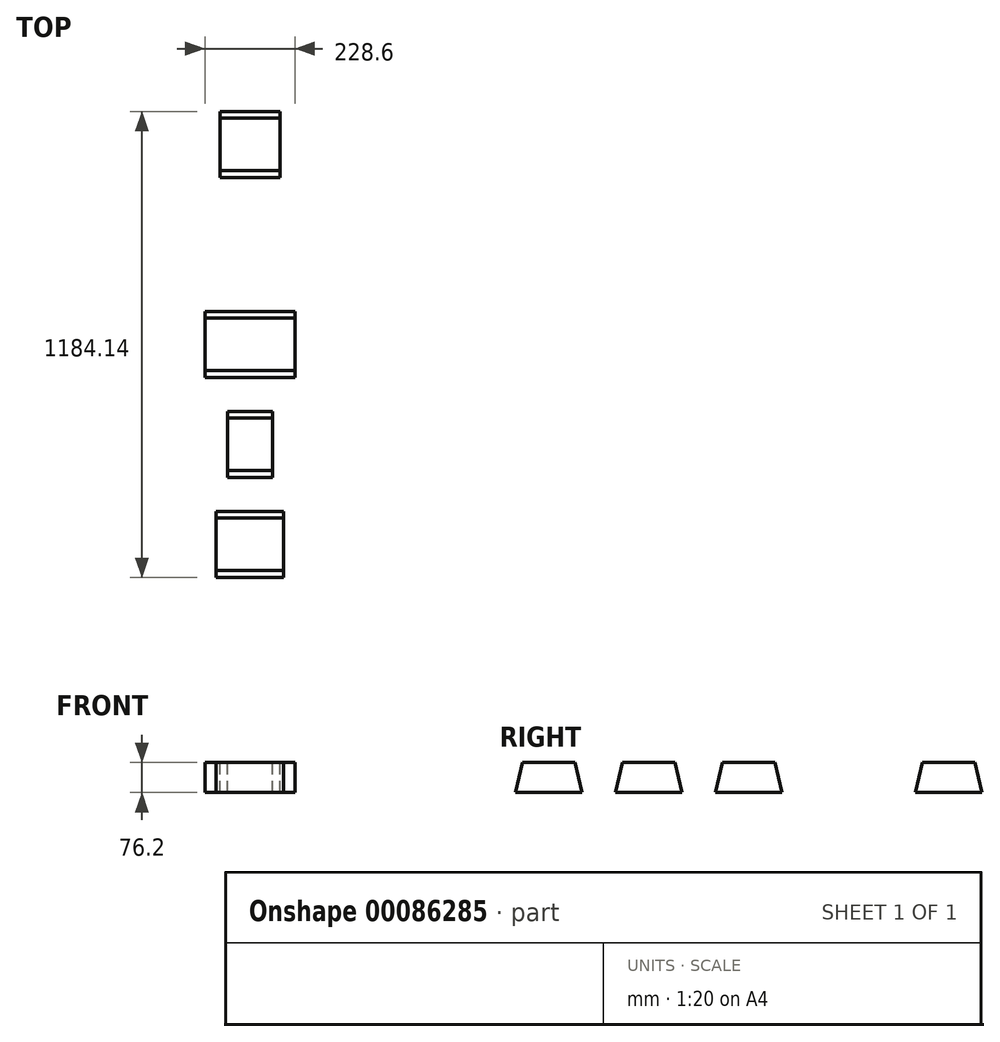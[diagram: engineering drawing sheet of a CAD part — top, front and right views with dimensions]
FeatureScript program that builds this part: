
annotation { "Feature Type Name" : "Feature", "Feature Type Description" : "" }
export const myFeature = defineFeature(function(context is Context, id is Id, definition is map)
    precondition{}
    {
        {
            var Q0;
            Q0=qCreatedBy(makeId("Top.planeOp"),FACE);
            var sketch = newSketch(context, id + "F0", { "sketchPlane" : qUnion([Q0])});
            skLineSegment(sketch, "E0.bottom", {"start": v(114.3, -84.07) * mm, "end": v(-114.3, -84.07) * mm});
            skLineSegment(sketch, "E0.top", {"start": v(114.3, 84.07) * mm, "end": v(-114.3, 84.07) * mm});
            skLineSegment(sketch, "E0.left", {"start": v(114.3, -84.07) * mm, "end": v(114.3, 84.07) * mm});
            skLineSegment(sketch, "E0.right", {"start": v(-114.3, -84.07) * mm, "end": v(-114.3, 84.07) * mm});
            skPoint(sketch, "E0.middle", {"position": v(0, 0) * mm});
            skLineSegment(sketch, "E1", {"start": v(0, 84.07) * mm, "end": v(0, -84.07) * mm, "construction": true});
            skLineSegment(sketch, "E2.bottom", {"start": v(-57.15, -169.93) * mm, "end": v(57.15, -169.93) * mm});
            skLineSegment(sketch, "E2.top", {"start": v(-57.15, -338.07) * mm, "end": v(57.15, -338.07) * mm});
            skLineSegment(sketch, "E2.left", {"start": v(-57.15, -169.93) * mm, "end": v(-57.15, -338.07) * mm});
            skLineSegment(sketch, "E2.right", {"start": v(57.15, -169.93) * mm, "end": v(57.15, -338.07) * mm});
            skPoint(sketch, "E2.middle", {"position": v(0, -254) * mm});
            skLineSegment(sketch, "E3", {"start": v(0, 0) * mm, "end": v(-114.3, 0) * mm, "construction": true});
            skLineSegment(sketch, "E4", {"start": v(-57.15, 0) * mm, "end": v(-57.15, -84.07) * mm, "construction": true});
            skLineSegment(sketch, "E5", {"start": v(-57.15, -42.04) * mm, "end": v(114.3, -42.04) * mm, "construction": true});
            skLineSegment(sketch, "E6.bottom", {"start": v(-85.72, -423.93) * mm, "end": v(85.73, -423.93) * mm});
            skLineSegment(sketch, "E6.top", {"start": v(-85.73, -592.07) * mm, "end": v(85.73, -592.07) * mm});
            skLineSegment(sketch, "E6.left", {"start": v(-85.72, -423.93) * mm, "end": v(-85.73, -592.07) * mm});
            skLineSegment(sketch, "E6.right", {"start": v(85.73, -423.93) * mm, "end": v(85.73, -592.07) * mm});
            skPoint(sketch, "E6.middle", {"position": v(0, -508) * mm});
            skPoint(sketch, "E6.middle.positionSnap0", {"position": v(0, -338.07) * mm});
            skPoint(sketch, "E6.centerSnap0", {"position": v(0, -338.07) * mm});
            skLineSegment(sketch, "E7", {"start": v(-38.1, 84.07) * mm, "end": v(-38.1, -84.07) * mm, "construction": true});
            skLineSegment(sketch, "E8", {"start": v(38.1, 84.07) * mm, "end": v(38.1, -84.07) * mm, "construction": true});
            skLineSegment(sketch, "E9", {"start": v(-114.3, 38.22) * mm, "end": v(-38.1, 38.22) * mm, "construction": true});
            skLineSegment(sketch, "E10", {"start": v(-38.1, 38.22) * mm, "end": v(38.1, 38.22) * mm, "construction": true});
            skLineSegment(sketch, "E11", {"start": v(38.1, 38.22) * mm, "end": v(114.3, 38.22) * mm, "construction": true});
            skLineSegment(sketch, "E12.bottom", {"start": v(76.2, 423.93) * mm, "end": v(0, 423.93) * mm});
            skLineSegment(sketch, "E12.top", {"start": v(76.2, 592.07) * mm, "end": v(-76.2, 592.07) * mm});
            skLineSegment(sketch, "E12.left", {"start": v(76.2, 423.93) * mm, "end": v(76.2, 592.07) * mm});
            skLineSegment(sketch, "E12.right", {"start": v(-76.2, 423.93) * mm, "end": v(-76.2, 592.07) * mm});
            skPoint(sketch, "E12.middle", {"position": v(0, 508) * mm});
            skLineSegment(sketch, "E13", {"start": v(0, 592.07) * mm, "end": v(0, 423.93) * mm, "construction": true});
            skLineSegment(sketch, "E14", {"start": v(0, 423.93) * mm, "end": v(-76.2, 423.93) * mm});
            skSolve(sketch);
        }
        {
            var Q0;
            Q0=makeQuery(id+"F0.imprint","IMPRINT",FACE,{"disambiguationData":[TD([[makeQuery(id+"F0.imprint","IMPRINT",EDGE,{"derivedFrom":sQuery(id+"F0.wireOp",EDGE,"E0.bottom")}),-1.0]])]});
            cPlane(context, id + "F1", {"entities" : qUnion([Q0]), "cplaneType" : CPlaneType.OFFSET, "offset" : 76.2 * mm, "width" : 152.4 * mm, "height" : 152.4 * mm});
        }
        {
            var Q0;
            Q0=qCreatedBy(id+"F1.planeOp",FACE);
            var sketch = newSketch(context, id + "F2", { "sketchPlane" : qUnion([Q0])});
            skLineSegment(sketch, "E15.bottom", {"start": v(-114.3, 66.68) * mm, "end": v(114.3, 66.68) * mm});
            skLineSegment(sketch, "E15.top", {"start": v(-114.3, -66.68) * mm, "end": v(114.3, -66.68) * mm});
            skLineSegment(sketch, "E15.left", {"start": v(-114.3, 66.68) * mm, "end": v(-114.3, -66.68) * mm});
            skLineSegment(sketch, "E15.right", {"start": v(114.3, 66.68) * mm, "end": v(114.3, -66.68) * mm});
            skPoint(sketch, "E15.middle", {"position": v(0, 0) * mm});
            skLineSegment(sketch, "E16.bottom", {"start": v(-57.15, -187.33) * mm, "end": v(57.15, -187.33) * mm});
            skLineSegment(sketch, "E16.top", {"start": v(-57.15, -320.68) * mm, "end": v(57.15, -320.68) * mm});
            skLineSegment(sketch, "E16.left", {"start": v(-57.15, -187.33) * mm, "end": v(-57.15, -320.68) * mm});
            skLineSegment(sketch, "E16.right", {"start": v(57.15, -187.33) * mm, "end": v(57.15, -320.68) * mm});
            skPoint(sketch, "E16.middle", {"position": v(0, -254) * mm});
            skLineSegment(sketch, "E17", {"start": v(0, 66.68) * mm, "end": v(0, -66.68) * mm, "construction": true});
            skLineSegment(sketch, "E18", {"start": v(-114.3, 0) * mm, "end": v(0, 0) * mm, "construction": true});
            skLineSegment(sketch, "E19", {"start": v(-57.15, 0) * mm, "end": v(-57.15, -66.68) * mm, "construction": true});
            skLineSegment(sketch, "E20", {"start": v(-57.15, -33.34) * mm, "end": v(114.3, -33.34) * mm, "construction": true});
            skLineSegment(sketch, "E21.bottom", {"start": v(-85.72, -441.33) * mm, "end": v(85.73, -441.33) * mm});
            skLineSegment(sketch, "E21.top", {"start": v(-85.73, -574.68) * mm, "end": v(85.72, -574.68) * mm});
            skLineSegment(sketch, "E21.left", {"start": v(-85.72, -441.33) * mm, "end": v(-85.73, -574.68) * mm});
            skLineSegment(sketch, "E21.right", {"start": v(85.73, -441.33) * mm, "end": v(85.72, -574.68) * mm});
            skPoint(sketch, "E21.middle", {"position": v(0, -508) * mm});
            skLineSegment(sketch, "E22", {"start": v(-38.1, 66.68) * mm, "end": v(-38.1, -66.68) * mm, "construction": true});
            skLineSegment(sketch, "E23", {"start": v(38.1, 66.68) * mm, "end": v(38.1, -66.68) * mm, "construction": true});
            skLineSegment(sketch, "E24", {"start": v(-114.3, 29.5) * mm, "end": v(-38.1, 29.5) * mm, "construction": true});
            skLineSegment(sketch, "E25", {"start": v(-38.1, 29.5) * mm, "end": v(38.1, 29.5) * mm, "construction": true});
            skLineSegment(sketch, "E26", {"start": v(38.1, 29.5) * mm, "end": v(114.3, 29.5) * mm, "construction": true});
            skLineSegment(sketch, "E27.bottom", {"start": v(76.2, 441.32) * mm, "end": v(0, 441.32) * mm});
            skLineSegment(sketch, "E27.top", {"start": v(76.2, 574.68) * mm, "end": v(-76.2, 574.68) * mm});
            skLineSegment(sketch, "E27.left", {"start": v(76.2, 441.32) * mm, "end": v(76.2, 574.68) * mm});
            skLineSegment(sketch, "E27.right", {"start": v(-76.2, 441.32) * mm, "end": v(-76.2, 574.68) * mm});
            skPoint(sketch, "E27.middle", {"position": v(0, 508) * mm});
            skLineSegment(sketch, "E28", {"start": v(0, 574.68) * mm, "end": v(0, 441.32) * mm, "construction": true});
            skLineSegment(sketch, "E29", {"start": v(0, 441.32) * mm, "end": v(-76.2, 441.32) * mm});
            skSolve(sketch);
        }
        {
            var Q0;
            Q0=makeQuery(id+"F0.imprint","IMPRINT",FACE,{"disambiguationData":[TD([[makeQuery(id+"F0.imprint","IMPRINT",EDGE,{"derivedFrom":sQuery(id+"F0.wireOp",EDGE,"E0.bottom")}),-1.0]])]});
            var Q1;
            Q1=makeQuery(id+"F2.imprint","IMPRINT",FACE,{"disambiguationData":[TD([[makeQuery(id+"F2.imprint","IMPRINT",EDGE,{"derivedFrom":sQuery(id+"F2.wireOp",EDGE,"E15.bottom")}),-1.0]])]});
            loft(context, id + "F3", {"sheetProfilesArray" : [{ "sheetProfileEntities" : qUnion([Q0]) }, { "sheetProfileEntities" : qUnion([Q1]) }]});
        }
        {
            var Q0;
            Q0=makeQuery(id+"F0.imprint","IMPRINT",FACE,{"disambiguationData":[TD([[makeQuery(id+"F0.imprint","IMPRINT",EDGE,{"derivedFrom":sQuery(id+"F0.wireOp",EDGE,"E2.bottom")}),-1.0]])]});
            var Q1;
            Q1=makeQuery(id+"F2.imprint","IMPRINT",FACE,{"disambiguationData":[TD([[makeQuery(id+"F2.imprint","IMPRINT",EDGE,{"derivedFrom":sQuery(id+"F2.wireOp",EDGE,"E16.bottom")}),-1.0]])]});
            loft(context, id + "F4", {"sheetProfilesArray" : [{ "sheetProfileEntities" : qUnion([Q0]) }, { "sheetProfileEntities" : qUnion([Q1]) }]});
        }
        {
            var Q0;
            Q0=makeQuery(id+"F0.imprint","IMPRINT",FACE,{"disambiguationData":[TD([[makeQuery(id+"F0.imprint","IMPRINT",EDGE,{"derivedFrom":sQuery(id+"F0.wireOp",EDGE,"E6.bottom")}),-1.0]])]});
            var Q1;
            Q1=makeQuery(id+"F2.imprint","IMPRINT",FACE,{"disambiguationData":[TD([[makeQuery(id+"F2.imprint","IMPRINT",EDGE,{"derivedFrom":sQuery(id+"F2.wireOp",EDGE,"E21.bottom")}),-1.0]])]});
            loft(context, id + "F5", {"sheetProfilesArray" : [{ "sheetProfileEntities" : qUnion([Q0]) }, { "sheetProfileEntities" : qUnion([Q1]) }]});
        }
        {
            var Q0;
            Q0=makeQuery(id+"F0.imprint","IMPRINT",FACE,{"disambiguationData":[TD([[makeQuery(id+"F0.imprint","IMPRINT",EDGE,{"derivedFrom":sQuery(id+"F0.wireOp",EDGE,"E12.bottom")}),-1.0]])]});
            var Q1;
            Q1=makeQuery(id+"F2.imprint","IMPRINT",FACE,{"disambiguationData":[TD([[makeQuery(id+"F2.imprint","IMPRINT",EDGE,{"derivedFrom":sQuery(id+"F2.wireOp",EDGE,"E27.bottom")}),-1.0]])]});
            loft(context, id + "F6", {"sheetProfilesArray" : [{ "sheetProfileEntities" : qUnion([Q0]) }, { "sheetProfileEntities" : qUnion([Q1]) }]});
        }
    });
